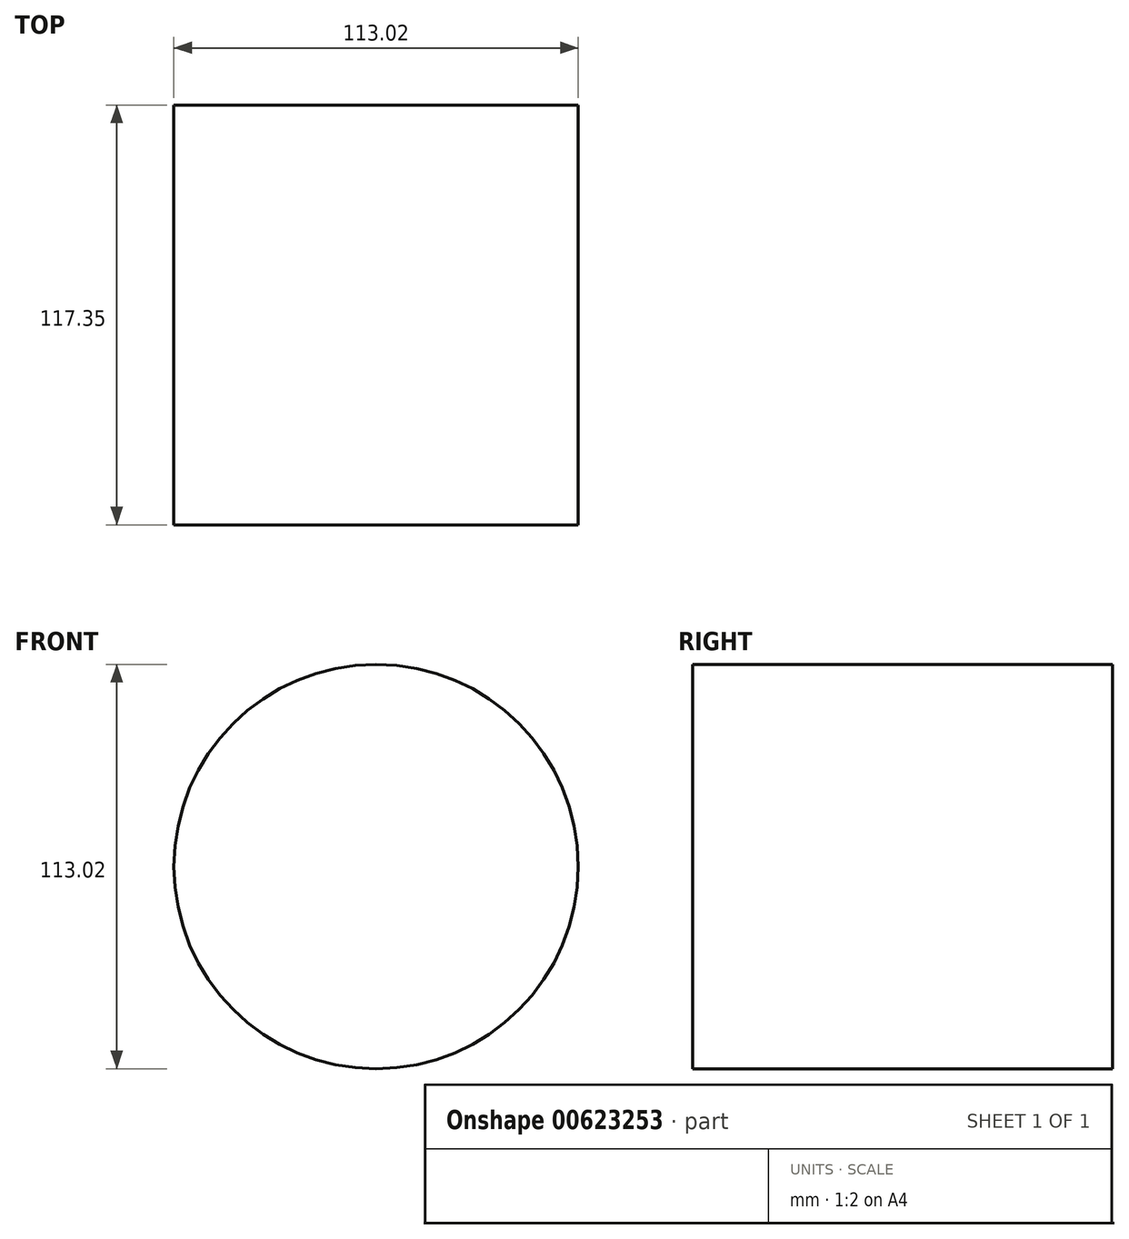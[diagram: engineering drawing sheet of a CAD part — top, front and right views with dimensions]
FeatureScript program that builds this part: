
annotation { "Feature Type Name" : "Feature", "Feature Type Description" : "" }
export const myFeature = defineFeature(function(context is Context, id is Id, definition is map)
    precondition{}
    {
        {
            var Q0;
            Q0=qCreatedBy(makeId("Front.planeOp"),FACE);
            var sketch = newSketch(context, id + "F0", { "sketchPlane" : qUnion([Q0])});
            skCircle(sketch, "E0", {"center": v(0, 0) * mm, "radius": 56.51 * mm});
            skSolve(sketch);
        }
        {
            var Q0;
            Q0=makeQuery(id+"F0.imprint","IMPRINT",FACE,{"disambiguationData":[TD([[makeQuery(id+"F0.imprint","IMPRINT",EDGE,{"derivedFrom":sQuery(id+"F0.wireOp",EDGE,"E0")}),1.0]])]});
            extrude(context, id + "F1", {"entities" : qUnion([Q0]), "depth" : 117.35 * mm, "offsetDistance" : 25.4 * mm});
        }
    });
